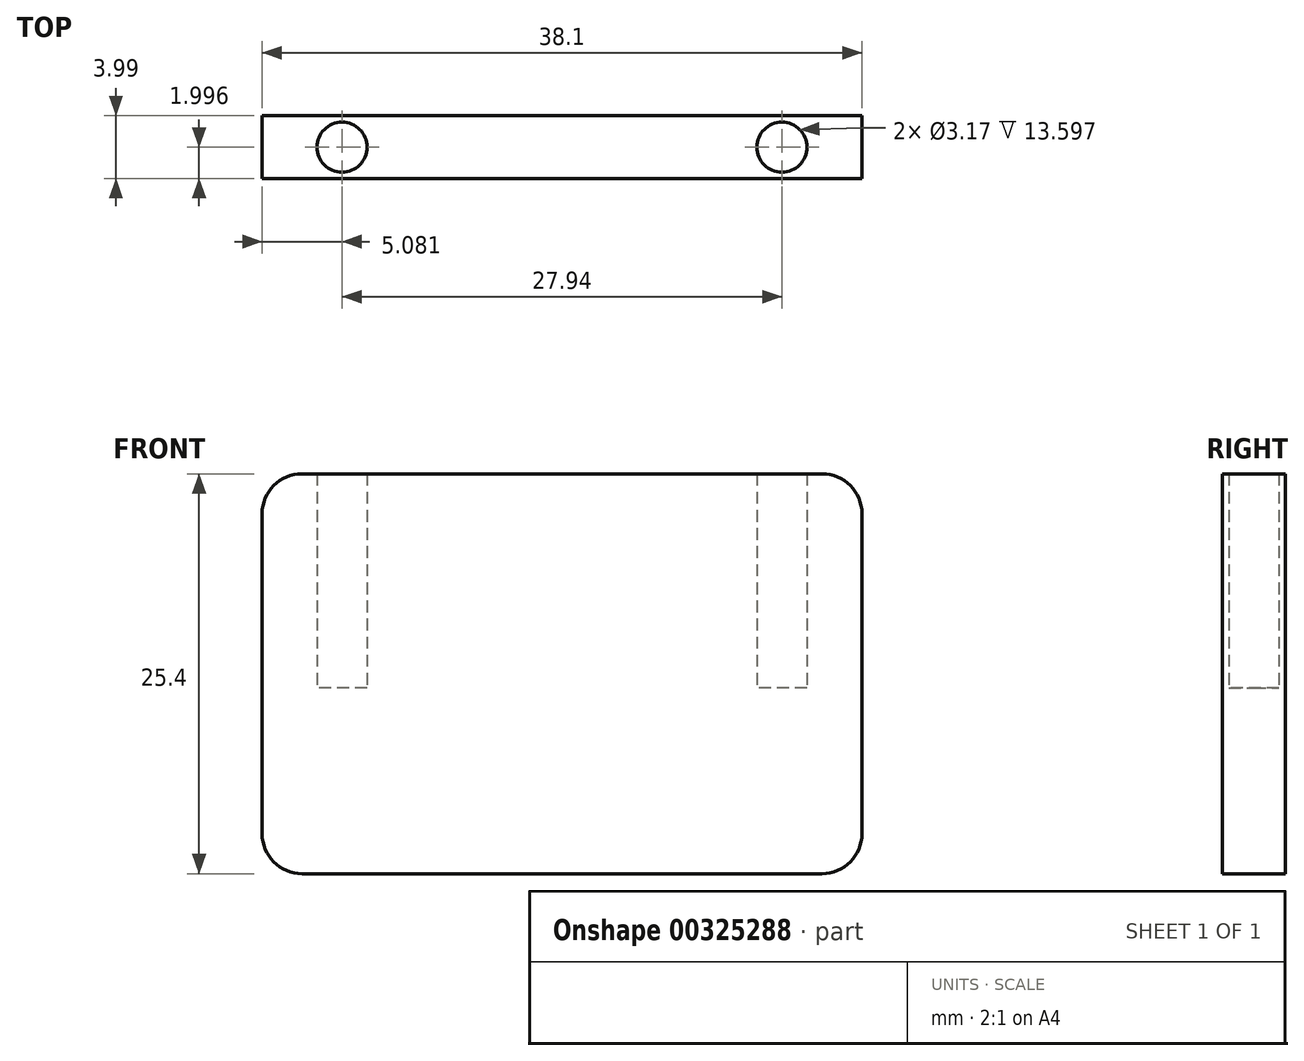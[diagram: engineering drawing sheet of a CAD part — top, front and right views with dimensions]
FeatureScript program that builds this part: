
annotation { "Feature Type Name" : "Feature", "Feature Type Description" : "" }
export const myFeature = defineFeature(function(context is Context, id is Id, definition is map)
    precondition{}
    {
        {
            var Q0;
            Q0=qCreatedBy(makeId("Front.planeOp"),FACE);
            var sketch = newSketch(context, id + "F0", { "sketchPlane" : qUnion([Q0])});
            skLineSegment(sketch, "E0", {"start": v(-32.23, 10.42) * mm, "end": v(-32.23, -14.98) * mm});
            skLineSegment(sketch, "E1", {"start": v(-32.23, 10.42) * mm, "end": v(5.87, 10.42) * mm});
            skLineSegment(sketch, "E2", {"start": v(-32.23, -14.98) * mm, "end": v(5.87, -14.98) * mm});
            skLineSegment(sketch, "E3", {"start": v(5.87, 10.42) * mm, "end": v(5.87, -14.98) * mm});
            skSolve(sketch);
        }
        {
            var Q0;
            Q0=makeQuery(id+"F0.imprint","IMPRINT",FACE,{"disambiguationData":[TD([[makeQuery(id+"F0.imprint","IMPRINT",EDGE,{"derivedFrom":sQuery(id+"F0.wireOp",EDGE,"E0")}),1.0]])]});
            extrude(context, id + "F1", {"entities" : qUnion([Q0]), "depth" : 4 * mm});
        }
        {
            var Q0;
            Q0=makeQuery(id+"F1.opExtrude","SWEPT_EDGE",EDGE,{"disambiguationData":[OSD([sQuery(id+"F0.wireOp",EDGE,"E0"),sQuery(id+"F0.wireOp",EDGE,"E2")])]});
            fillet(context, id + "F2", {"entities" : qUnion([Q0]), "radius" : 2.54 * mm, "tangentPropagation" : true, "allowEdgeOverflow" : false});
        }
        {
            var Q0;
            Q0=makeQuery(id+"F1.opExtrude","SWEPT_EDGE",EDGE,{"disambiguationData":[OSD([sQuery(id+"F0.wireOp",EDGE,"E2"),sQuery(id+"F0.wireOp",EDGE,"E3")])]});
            fillet(context, id + "F3", {"entities" : qUnion([Q0]), "radius" : 2.54 * mm, "tangentPropagation" : true, "allowEdgeOverflow" : false});
        }
        {
            var Q0;
            Q0=makeQuery(id+"F1.opExtrude","SWEPT_EDGE",EDGE,{"disambiguationData":[OSD([sQuery(id+"F0.wireOp",EDGE,"E0"),sQuery(id+"F0.wireOp",EDGE,"E1")])]});
            fillet(context, id + "F4", {"entities" : qUnion([Q0]), "radius" : 2.54 * mm, "tangentPropagation" : true, "allowEdgeOverflow" : false});
        }
        {
            var Q0;
            Q0=makeQuery(id+"F1.opExtrude","SWEPT_EDGE",EDGE,{"disambiguationData":[OSD([sQuery(id+"F0.wireOp",EDGE,"E1"),sQuery(id+"F0.wireOp",EDGE,"E3")])]});
            fillet(context, id + "F5", {"entities" : qUnion([Q0]), "radius" : 2.54 * mm, "tangentPropagation" : true, "allowEdgeOverflow" : false});
        }
        {
            var Q0;
            Q0=qCreatedBy(makeId("Top.planeOp"),FACE);
            var sketch = newSketch(context, id + "F6", { "sketchPlane" : qUnion([Q0])});
            skCircle(sketch, "E4", {"center": v(-27.15, -2) * mm, "radius": 1.59 * mm});
            skCircle(sketch, "E5", {"center": v(0.8, -2) * mm, "radius": 1.59 * mm});
            skSolve(sketch);
        }
        {
            var Q0;
            Q0 = qSketchRegion(id + "F6", true);
            var Q1;
            Q1=makeQuery(id+"F1.opExtrude","SWEPT_FACE",FACE,{"disambiguationData":[OSD([sQuery(id+"F0.wireOp",EDGE,"E1")])]});
            extrude(context, id + "F7", {"entities" : qUnion([Q0]), "operationType" : NewBodyOperationType.REMOVE, "endBound" : BoundingType.UP_TO_SURFACE, "endBoundEntityFace" : qUnion([Q1]), "depth" : 3.17 * mm, "hasSecondDirection" : true, "secondDirectionOppositeDirection" : true, "secondDirectionDepth" : 3.17 * mm});
        }
    });
